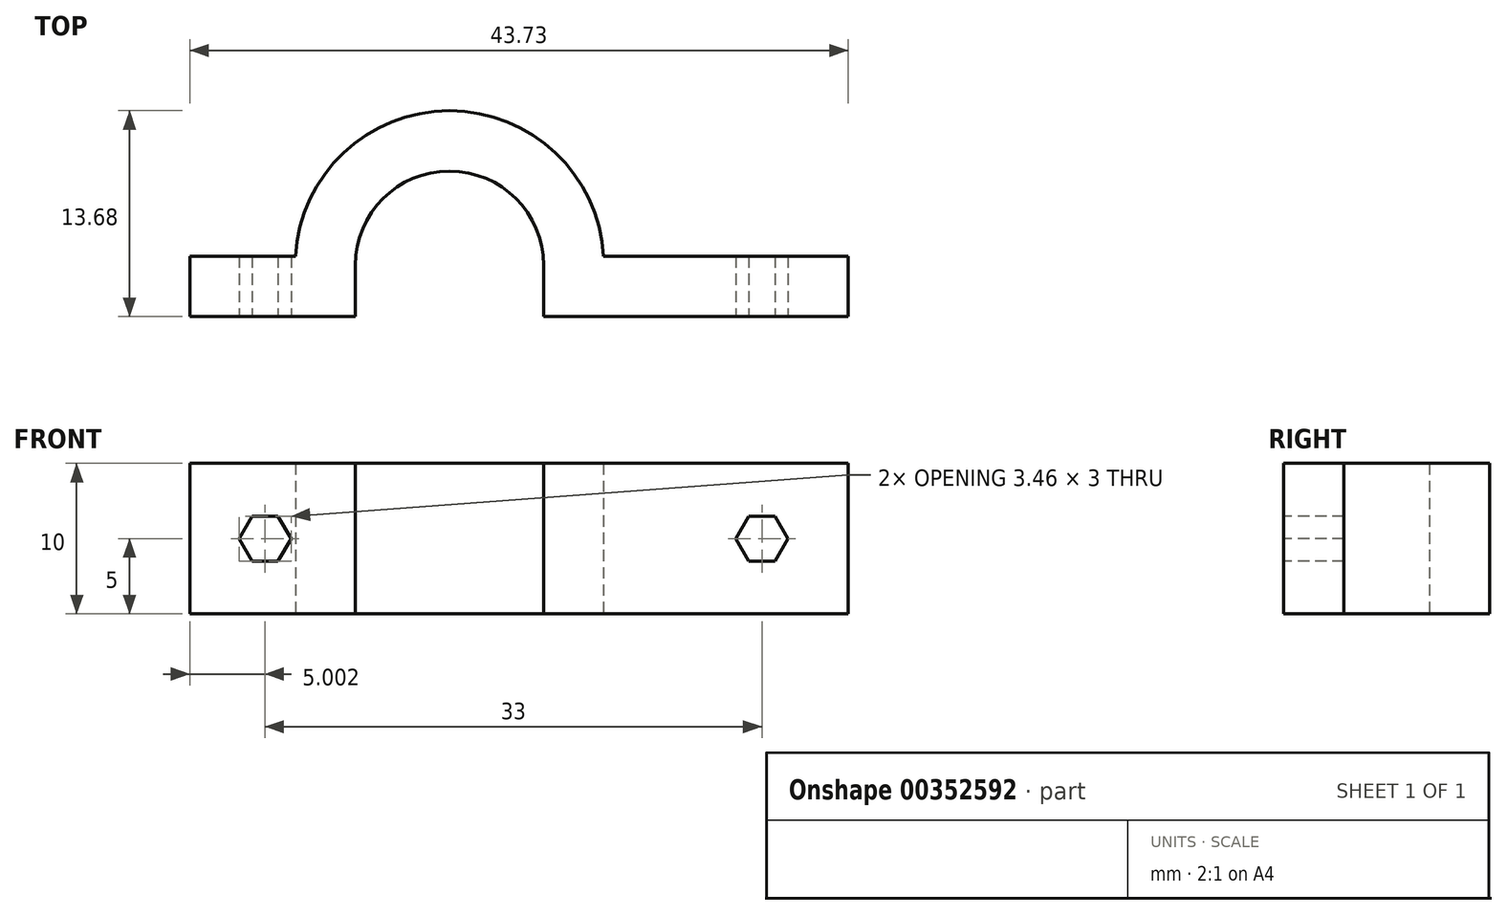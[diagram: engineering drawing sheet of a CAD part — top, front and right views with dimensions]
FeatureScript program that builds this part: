
annotation { "Feature Type Name" : "Feature", "Feature Type Description" : "" }
export const myFeature = defineFeature(function(context is Context, id is Id, definition is map)
    precondition{}
    {
        {
            var Q0;
            Q0=qCreatedBy(makeId("Top.planeOp"),FACE);
            var sketch = newSketch(context, id + "F0", { "sketchPlane" : qUnion([Q0])});
            skLineSegment(sketch, "E0", {"start": v(14.61, -13.31) * mm, "end": v(38.11, -13.31) * mm});
            skLineSegment(sketch, "E1", {"start": v(38.11, -13.31) * mm, "end": v(38.11, -9.31) * mm});
            skLineSegment(sketch, "E2", {"start": v(38.11, -9.31) * mm, "end": v(18.6, -9.31) * mm});
            skLineSegment(sketch, "E3", {"start": v(14.61, -13.31) * mm, "end": v(2.11, -13.31) * mm, "construction": true});
            skLineSegment(sketch, "E4", {"start": v(2.11, -13.31) * mm, "end": v(-8.89, -13.31) * mm});
            skLineSegment(sketch, "E5", {"start": v(-8.89, -13.31) * mm, "end": v(-8.89, -9.31) * mm});
            skLineSegment(sketch, "E6", {"start": v(-8.89, -9.31) * mm, "end": v(-1.87, -9.31) * mm});
            skLineSegment(sketch, "E7", {"start": v(14.61, -13.31) * mm, "end": v(14.61, -9.9) * mm});
            skLineSegment(sketch, "E8", {"start": v(2.11, -13.31) * mm, "end": v(2.11, -9.9) * mm});
            skArc(sketch, "E9", {"start": v(14.61, -9.9) * mm, "mid": v(8.36, -3.64) * mm, "end": v(2.11, -9.9) * mm});
            skArc(sketch, "E10", {"start": v(18.6, -9.31) * mm, "mid": v(8.36, 0.37) * mm, "end": v(-1.87, -9.31) * mm});
            skSolve(sketch);
        }
        {
            var Q0;
            Q0 = qSketchRegion(id + "F0", true);
            extrude(context, id + "F1", {"entities" : qUnion([Q0]), "depth" : 10 * mm});
        }
        {
            var Q0;
            Q0=makeQuery(id+"F1.opExtrude","SWEPT_FACE",FACE,{"disambiguationData":[OSD([sQuery(id+"F0.wireOp",EDGE,"E4")])]});
            var sketch = newSketch(context, id + "F2", { "sketchPlane" : qUnion([Q0])});
            skCircle(sketch, "E11.cCircle", {"center": v(-3.89, 5) * mm, "radius": 1.5 * mm, "construction": true});
            skLineSegment(sketch, "E11.0", {"start": v(-3.02, 6.5) * mm, "end": v(-2.16, 5) * mm});
            skLineSegment(sketch, "E11.1", {"start": v(-2.16, 5) * mm, "end": v(-3.02, 3.5) * mm});
            skLineSegment(sketch, "E11.2", {"start": v(-3.02, 3.5) * mm, "end": v(-4.75, 3.5) * mm});
            skLineSegment(sketch, "E11.3", {"start": v(-4.75, 3.5) * mm, "end": v(-5.62, 5) * mm});
            skLineSegment(sketch, "E11.4", {"start": v(-5.62, 5) * mm, "end": v(-4.75, 6.5) * mm});
            skLineSegment(sketch, "E11.5", {"start": v(-4.75, 6.5) * mm, "end": v(-3.02, 6.5) * mm});
            skPoint(sketch, "E11.0.midPoint", {"position": v(-2.59, 5.75) * mm});
            skCircle(sketch, "E12.cCircle", {"center": v(29.11, 5) * mm, "radius": 1.5 * mm, "construction": true});
            skLineSegment(sketch, "E12.0", {"start": v(28.25, 6.5) * mm, "end": v(29.98, 6.5) * mm});
            skLineSegment(sketch, "E12.1", {"start": v(29.98, 6.5) * mm, "end": v(30.84, 5) * mm});
            skLineSegment(sketch, "E12.2", {"start": v(30.84, 5) * mm, "end": v(29.98, 3.5) * mm});
            skLineSegment(sketch, "E12.3", {"start": v(29.98, 3.5) * mm, "end": v(28.25, 3.5) * mm});
            skLineSegment(sketch, "E12.4", {"start": v(28.25, 3.5) * mm, "end": v(27.38, 5) * mm});
            skLineSegment(sketch, "E12.5", {"start": v(27.38, 5) * mm, "end": v(28.25, 6.5) * mm});
            skPoint(sketch, "E12.0.midPoint", {"position": v(29.11, 6.5) * mm});
            skLineSegment(sketch, "E13", {"start": v(-5.62, 5) * mm, "end": v(30.84, 5) * mm, "construction": true});
            skSolve(sketch);
        }
        {
            var Q0;
            Q0 = qSketchRegion(id + "F2", true);
            extrude(context, id + "F3", {"entities" : qUnion([Q0]), "operationType" : NewBodyOperationType.REMOVE, "endBound" : BoundingType.THROUGH_ALL, "oppositeDirection" : true, "depth" : 25 * mm});
        }
        {
            var Q0;
            Q0=makeQuery(id+"F1.opExtrude","SWEPT_FACE",FACE,{"disambiguationData":[OSD([sQuery(id+"F0.wireOp",EDGE,"E1")])]});
            extrude(context, id + "F4", {"entities" : qUnion([Q0]), "operationType" : NewBodyOperationType.REMOVE, "oppositeDirection" : true, "depth" : 3.27 * mm});
        }
    });
